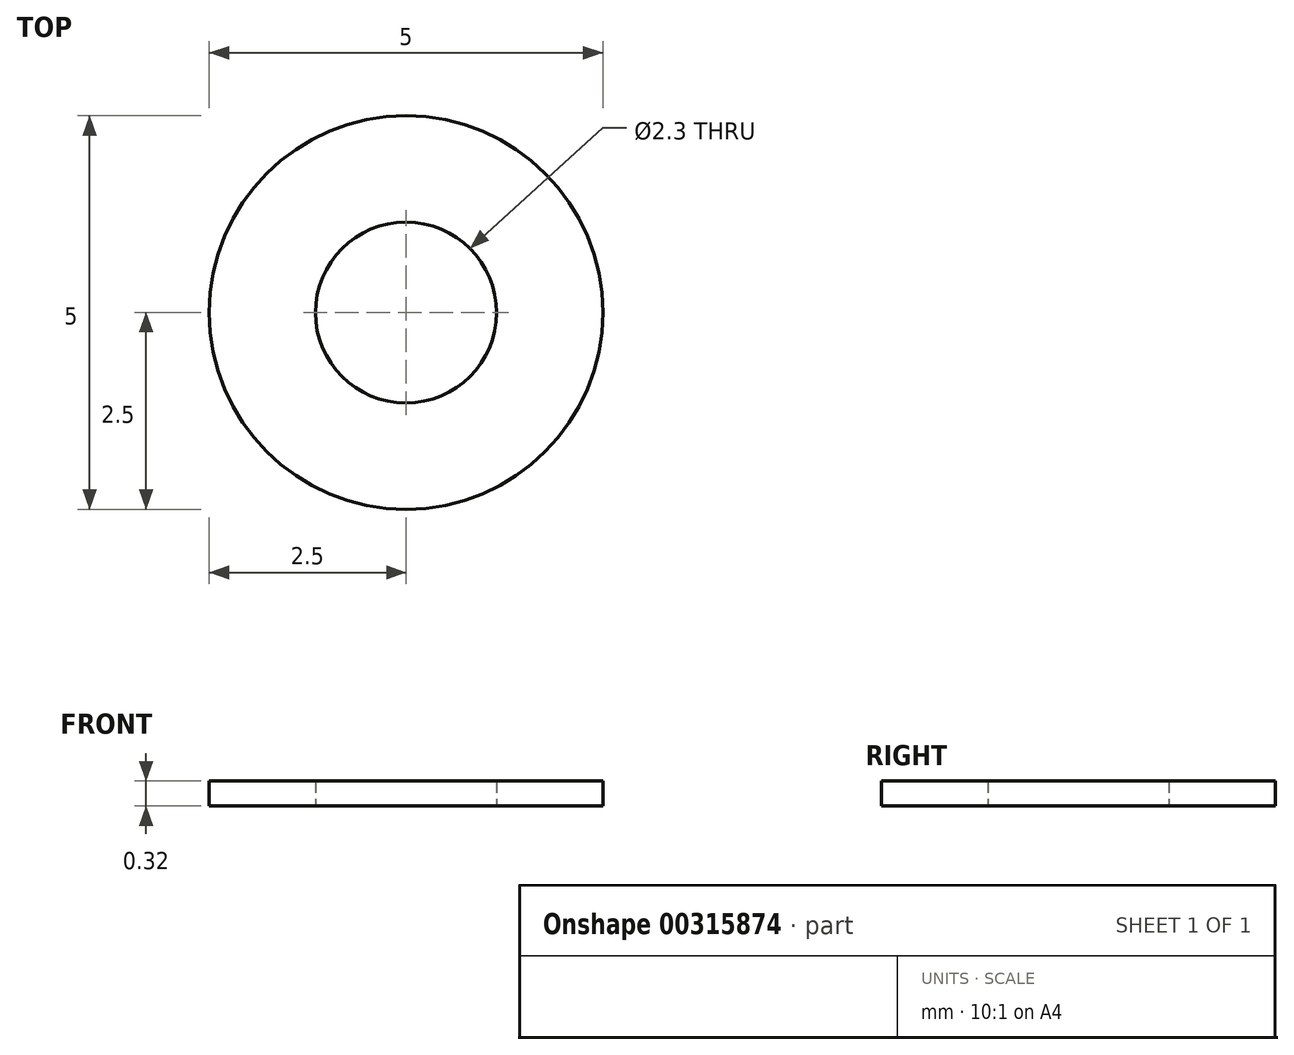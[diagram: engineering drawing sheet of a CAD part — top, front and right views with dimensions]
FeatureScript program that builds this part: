
annotation { "Feature Type Name" : "Feature", "Feature Type Description" : "" }
export const myFeature = defineFeature(function(context is Context, id is Id, definition is map)
    precondition{}
    {
        {
            var Q0;
            Q0=qCreatedBy(makeId("Top.planeOp"),FACE);
            var sketch = newSketch(context, id + "F0", { "sketchPlane" : qUnion([Q0])});
            skCircle(sketch, "E0", {"center": v(0, 0) * mm, "radius": 2.5 * mm});
            skCircle(sketch, "E1", {"center": v(0, 0) * mm, "radius": 1.15 * mm});
            skSolve(sketch);
        }
        {
            var Q0;
            Q0=makeQuery(id+"F0.imprint","IMPRINT",FACE,{"disambiguationData":[TD([[makeQuery(id+"F0.imprint","IMPRINT",EDGE,{"derivedFrom":sQuery(id+"F0.wireOp",EDGE,"E0")}),1.0]])]});
            extrude(context, id + "F1", {"entities" : qUnion([Q0]), "depth" : 0.32 * mm});
        }
    });
